# Revit family: Equipment-Gym-Draper_Inc.-Roll_Up_Gym_Divider
name_source: partatom
category: Specialty Equipment
revit_build: Autodesk Revit Architecture 2012 (Build: 20110309_2315(x64)
units: mm (PartAtom-declared; Revit-internal decimal feet)

## types (2) — shared parameters
Apparent Load = 560 VA
Constraint Height = 20' - 0"
Description = Gym Divider
Frequency = 60 Hz
Height = 20' - 0"
Manufacturer = Draper Inc.
Model = Roll-Up Gym Dividers
Number of Poles = 1
Phase = 1
Power Factor = 1
Product Documentation Link = http://www.draperinc.com
Product Name = Roll-Up Gym Dividers
Product Page URL = http://www.draperinc.com
Spacing = 15' - 0"
URL = http://www.draperinc.com
Vinyl = Fabric - Draper Inc. - Vinyl
Vinyl Height = 6' - 0"
Voltage = 120 V

## per-type parameters (varying)
| type | Mesh | Vinyl & Net |
| Solid Vinyl | Fabric - Draper Inc. - Vinyl | No |
| Vinyl & Mesh Combo | Fabric - Draper Inc. - Mesh | Yes |

type visibility flags (boolean, named after types; folded from table):
- Solid Vinyl: Yes: Solid Vinyl
- Vinyl & Mesh Combo: Yes: (none)

## geometry (parser evidence)
native form markers: Blend x16, Sweep x12
no freeform markers — native parametric forms only
